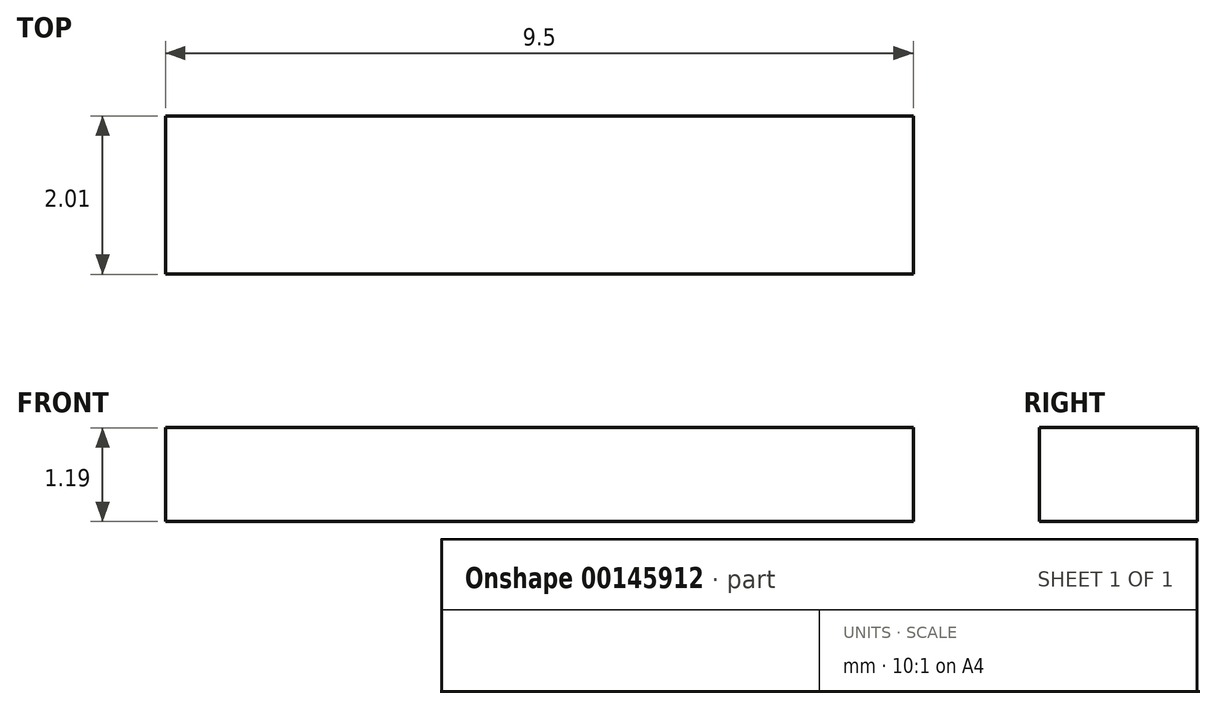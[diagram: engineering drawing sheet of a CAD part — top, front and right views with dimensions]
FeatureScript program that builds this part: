
annotation { "Feature Type Name" : "Feature", "Feature Type Description" : "" }
export const myFeature = defineFeature(function(context is Context, id is Id, definition is map)
    precondition{}
    {
        {
            var Q0;
            Q0=qCreatedBy(makeId("Top.planeOp"),FACE);
            var sketch = newSketch(context, id + "F0", { "sketchPlane" : qUnion([Q0])});
            skLineSegment(sketch, "E0.bottom", {"start": v(0, 0) * mm, "end": v(9.5, 0) * mm});
            skLineSegment(sketch, "E0.top", {"start": v(0, -2) * mm, "end": v(9.5, -2) * mm});
            skLineSegment(sketch, "E0.left", {"start": v(0, 0) * mm, "end": v(0, -2) * mm});
            skLineSegment(sketch, "E0.right", {"start": v(9.5, 0) * mm, "end": v(9.5, -2) * mm});
            skSolve(sketch);
        }
        {
            var Q0;
            Q0 = qSketchRegion(id + "F0", true);
            extrude(context, id + "F1", {"entities" : qUnion([Q0]), "depth" : 1.2 * mm});
        }
    });
